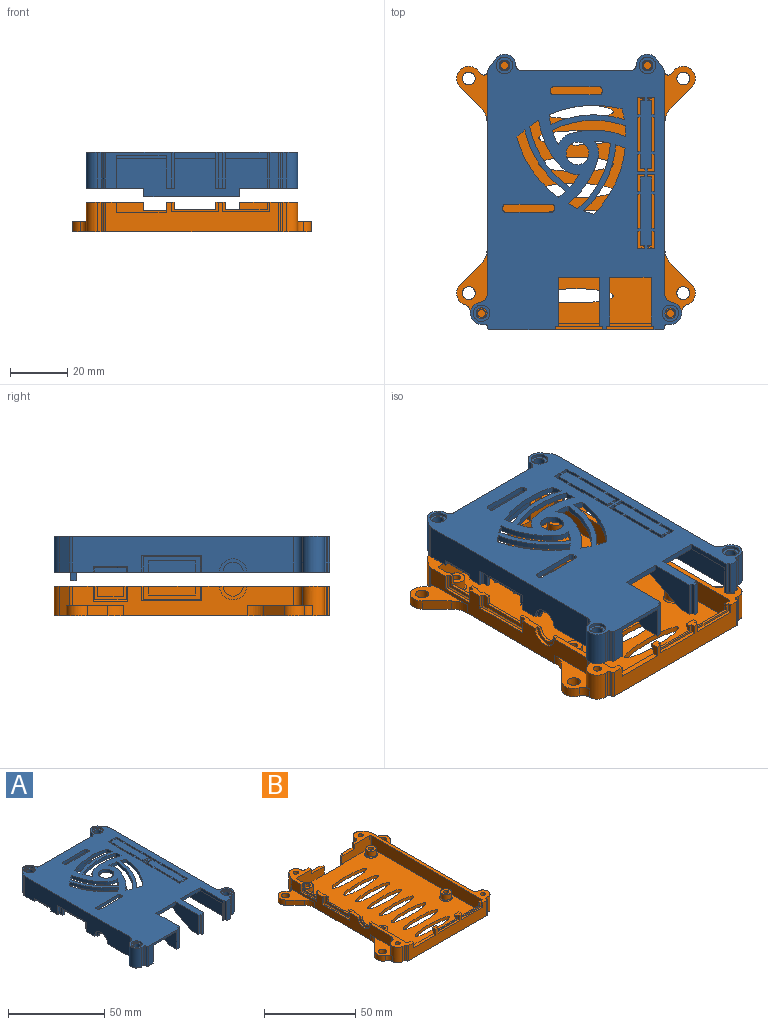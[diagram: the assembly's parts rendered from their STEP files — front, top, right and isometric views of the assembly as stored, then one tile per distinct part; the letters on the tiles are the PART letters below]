
ASSEMBLY  parts=2 mates=1
PART A: 207 faces, bbox 73.8x96.3x15.5 mm
  f0: plane 96.25x73.8mm, normal (0,0,1), area 4343.7mm2, adj f1,f2,f3,f4,f5,f6,f8,f9
  f1: cylinder r=38.11mm len=2.81mm, axis (0,0,1), area 7.6mm2, adj f0,f3,f6,f7
  f2: cylinder r=38.11mm len=3.17mm, axis (0,0,1), area 7.6mm2, adj f0,f7,f27,f28
  f3: cylinder r=34.77mm len=21.39mm, axis (0,0,-1), area 52.8mm2, adj f0,f1,f4,f7
  f4: cylinder r=25.5mm len=2.73mm, axis (0,0,1), area 7mm2, adj f0,f3,f6,f7
  f5: cylinder r=25.5mm len=4.42mm, axis (0,0,1), area 11.1mm2, adj f0,f7,f27,f29
  f6: cylinder r=38.11mm len=21mm, axis (0,0,1), area 52mm2, adj f0,f1,f4,f7
  f7: plane 86.6x58mm, normal (0,0,-1), area 3024.7mm2, adj f1,f2,f3,f4,f5,f6,f8,f9
  f8: cylinder r=38.11mm len=3.71mm, axis (0,0,1), area 7.6mm2, adj f0,f7,f10,f13
  f9: cylinder r=38.11mm len=3.78mm, axis (0,0,1), area 7.6mm2, adj f0,f7,f14,f16
  f10: cylinder r=34.77mm len=25.71mm, axis (0,0,-1), area 52.8mm2, adj f0,f7,f8,f11
  f11: cylinder r=25.5mm len=3.44mm, axis (0,0,1), area 7mm2, adj f0,f7,f10,f13
  f12: cylinder r=25.5mm len=5.08mm, axis (0,0,1), area 11.1mm2, adj f0,f7,f14,f15
  f13: cylinder r=38.11mm len=25.42mm, axis (0,0,1), area 52mm2, adj f0,f7,f8,f11
  f14: cylinder r=32.83mm len=25.5mm, axis (0,0,-1), area 52.5mm2, adj f0,f7,f9,f12
  f15: cylinder r=7.38mm len=4.78mm, axis (0,0,1), area 12.9mm2, adj f0,f7,f12,f16
  f16: cylinder r=29.38mm len=18.77mm, axis (0,0,1), area 38.3mm2, adj f0,f7,f9,f15
  f17: cylinder r=38.11mm len=3.62mm, axis (0,0,1), area 7.6mm2, adj f0,f7,f19,f22
  f18: cylinder r=38.11mm len=3.38mm, axis (0,0,1), area 7.6mm2, adj f0,f7,f23,f25
  f19: cylinder r=34.77mm len=23.14mm, axis (0,0,-1), area 52.8mm2, adj f0,f7,f17,f20
  f20: cylinder r=25.5mm len=3.24mm, axis (0,0,1), area 7mm2, adj f0,f7,f19,f22
  f21: cylinder r=25.5mm len=5.48mm, axis (0,0,1), area 11.1mm2, adj f0,f7,f23,f24
  f22: cylinder r=38.11mm len=23.03mm, axis (0,0,1), area 52mm2, adj f0,f7,f17,f20
  f23: cylinder r=32.83mm len=22.84mm, axis (0,0,-1), area 52.5mm2, adj f0,f7,f18,f21
  f24: cylinder r=7.38mm len=6.15mm, axis (0,0,1), area 12.9mm2, adj f0,f7,f21,f25
  f25: cylinder r=29.38mm len=15.65mm, axis (0,0,1), area 38.3mm2, adj f0,f7,f18,f24
  f26: cylinder r=4mm len=8mm, axis (0,0,1), area 50.3mm2, adj f0,f7
  f27: cylinder r=32.83mm len=21.32mm, axis (0,0,-1), area 52.5mm2, adj f0,f2,f5,f7
  f28: cylinder r=29.38mm len=16.85mm, axis (0,0,1), area 38.3mm2, adj f0,f2,f7,f29
  f29: cylinder r=7.38mm len=5.88mm, axis (0,0,1), area 12.9mm2, adj f0,f5,f7,f28
  f30: plane 16x2mm, normal (0,-1,0), area 32mm2, adj f0,f7,f31,f37
  f31: cylinder r=1mm len=2mm, axis (0,0,-1), area 3.1mm2, adj f0,f7,f30,f32
  f32: plane 2x0.8mm, normal (-1,0,0), area 1.6mm2, adj f0,f7,f31,f33
  f33: cylinder r=1mm len=2mm, axis (0,0,-1), area 3.1mm2, adj f0,f7,f32,f34
  f34: plane 16x2mm, normal (0,1,0), area 32mm2, adj f0,f7,f33,f35
  f35: cylinder r=1mm len=2mm, axis (0,0,-1), area 3.1mm2, adj f0,f7,f34,f36
  f36: plane 2x0.8mm, normal (1,0,0), area 1.6mm2, adj f0,f7,f35,f37
  f37: cylinder r=1mm len=2mm, axis (0,0,-1), area 3.1mm2, adj f0,f7,f30,f36
  f38: plane 2x0.8mm, normal (-1,0,0), area 1.6mm2, adj f0,f7,f39,f45
  f39: cylinder r=1mm len=2mm, axis (0,0,-1), area 3.1mm2, adj f0,f7,f38,f40
  f40: plane 16x2mm, normal (0,1,0), area 32mm2, adj f0,f7,f39,f41
  f41: cylinder r=1mm len=2mm, axis (0,0,-1), area 3.1mm2, adj f0,f7,f40,f42
  f42: plane 2x0.8mm, normal (1,0,0), area 1.6mm2, adj f0,f7,f41,f43
  f43: cylinder r=1mm len=2mm, axis (0,0,-1), area 3.1mm2, adj f0,f7,f42,f44
  f44: plane 16x2mm, normal (0,-1,0), area 32mm2, adj f0,f7,f43,f45
  f45: cylinder r=1mm len=2mm, axis (0,0,-1), area 3.1mm2, adj f0,f7,f38,f44
  f46: cylinder r=1mm len=10.5mm, axis (0,0,-1), area 16.5mm2, adj f7,f47,f50,f55
  f47: plane 10.5x1.55mm, normal (0,1,0), area 16.3mm2, adj f7,f46,f50,f90
  f48: plane 10.5x1.75mm, normal (0,1,0), area 18.4mm2, adj f7,f51,f60,f100
  f49: plane 9.75x2.5mm, normal (0,0,-1), area 16.8mm2, adj f55,f104,f110,f111,f112,f113,f114,f115
  f50: plane 30.25x10.45mm, normal (0,0,-1), area 94.5mm2, adj f46,f47,f55,f82,f90,f103,f104,f105
  f51: plane 96.25x20.3mm, normal (0,0,-1), area 270.9mm2, adj f48,f57,f58,f59,f60,f61,f62,f69
  f52: plane 32.75x14.2mm, normal (0,0,-1), area 96.1mm2, adj f55,f56,f57,f62,f68,f104,f115,f116
  f53: plane 6x3.5mm, normal (0,0,-1), area 18.6mm2, adj f80,f83,f85,f93,f94,f95,f96,f98
  f54: plane 6x2.8mm, normal (0,0,-1), area 15.6mm2, adj f82,f84,f86,f87,f88,f102
  f55: plane 84.6x10.5mm, normal (1,0,0), area 682.2mm2, adj f7,f46,f49,f50,f52,f56,f112,f122
  f56: cylinder r=1mm len=10.5mm, axis (0,0,1), area 16.5mm2, adj f7,f52,f55,f57
  f57: plane 56x13.5mm, normal (0,-1,0), area 688.2mm2, adj f7,f51,f52,f56,f58,f61,f64,f68
  f58: cylinder r=1mm len=10.5mm, axis (0,0,1), area 16.5mm2, adj f7,f51,f57,f59
  f59: plane 84.6x10.5mm, normal (-1,0,0), area 888.3mm2, adj f7,f51,f58,f60
  f60: cylinder r=1mm len=10.5mm, axis (0,0,1), area 16.5mm2, adj f7,f48,f51,f59
  f61: plane 3x2mm, normal (1,0,0), area 6mm2, adj f51,f57,f62,f64
  f62: plane 38.21x15.5mm, normal (0,1,0), area 553.1mm2, adj f0,f51,f52,f61,f63,f64,f66,f67
  f63: plane 1.5x1mm, normal (1,0,0), area 1.5mm2, adj f62,f64,f65,f67
  f64: plane 33.4x2mm, normal (0,0,-1), area 50.3mm2, adj f57,f61,f62,f63,f65,f66,f68
  f65: plane 16.5x1.5mm, normal (0,1,0), area 24.7mm2, adj f63,f64,f66,f67
  f66: plane 1.5x1mm, normal (-1,0,0), area 1.5mm2, adj f62,f64,f65,f67
  f67: plane 16.5x1mm, normal (0,0,-1), area 16.5mm2, adj f62,f63,f65,f66
  f68: plane 3x2mm, normal (-1,0,0), area 6mm2, adj f52,f57,f62,f64
  f69: cylinder r=2mm len=12.5mm, axis (0,0,1), area 38.2mm2, adj f0,f51,f62,f70
  f70: cylinder r=3.9mm len=12.5mm, axis (0,0,1), area 121.2mm2, adj f0,f51,f69,f71
  f71: plane 12.5x3.48mm, normal (0.82,0.58,0), area 53.1mm2, adj f0,f51,f70,f72
  f72: cylinder r=2mm len=12.5mm, axis (0,0,1), area 15.3mm2, adj f0,f51,f71,f73
  f73: plane 77.46x12.5mm, normal (1,0,0), area 968.2mm2, adj f0,f51,f72,f75
  f74: plane 12.5x0.18mm, normal (1,0,0), area 2.3mm2, adj f0,f51,f78,f79
  f75: cylinder r=3mm len=12.5mm, axis (0,0,1), area 53.5mm2, adj f0,f51,f73,f76
  f76: cylinder r=3.9mm len=12.5mm, axis (0,0,1), area 146.1mm2, adj f0,f51,f75,f77
  f77: plane 12.5x1.2mm, normal (0,-1,0), area 15mm2, adj f0,f51,f76,f78
  f78: cylinder r=0.8mm len=12.5mm, axis (0,0,-1), area 15.7mm2, adj f0,f51,f74,f77
  f79: cylinder r=0.8mm len=12.5mm, axis (0,0,-1), area 15.7mm2, adj f0,f51,f74,f81
  f80: plane 12.5x1.5mm, normal (0,-1,0), area 18.8mm2, adj f0,f53,f83,f98
  f81: plane 12.5x2.95mm, normal (0,-1,0), area 36.9mm2, adj f0,f51,f79,f99
  f82: plane 22.95x12.5mm, normal (0,-1,0), area 90.3mm2, adj f0,f50,f54,f88,f90,f91,f102,f103
  f83: plane 12.5x1.2mm, normal (-1,0,0), area 15mm2, adj f0,f53,f80,f85
  f84: plane 12.5x1mm, normal (0,-1,0), area 12.5mm2, adj f0,f54,f86,f102
  f85: plane 12.5x1mm, normal (0,-1,0), area 12.5mm2, adj f0,f53,f83,f93
  f86: plane 25.8x12.5mm, normal (1,0,0), area 194.7mm2, adj f0,f7,f54,f84,f87,f92
  f87: plane 21x10.5mm, normal (0,0.45,-0.89), area 65.7mm2, adj f7,f54,f86,f88
  f88: plane 27x11.3mm, normal (-1,0,0), area 191.4mm2, adj f7,f54,f82,f87,f89,f91
  f89: plane 17.4x0.8mm, normal (0,-1,0), area 13.9mm2, adj f7,f88,f90,f91
  f90: plane 22.7x11.3mm, normal (1,0,0), area 39.2mm2, adj f7,f47,f50,f82,f89,f91
  f91: plane 22.7x17.4mm, normal (0,0,-1), area 395mm2, adj f82,f88,f89,f90
  f92: plane 14.5x2mm, normal (0,-1,0), area 29mm2, adj f0,f7,f86,f93
  f93: plane 25.8x12.5mm, normal (-1,0,0), area 194.7mm2, adj f0,f7,f53,f85,f92,f94
  f94: plane 21x10.5mm, normal (0,0.45,-0.89), area 82.2mm2, adj f7,f53,f93,f95
  f95: plane 25.8x12.5mm, normal (1,0,0), area 194.7mm2, adj f0,f7,f53,f94,f96,f101
  f96: plane 12.5x1mm, normal (0,-1,0), area 12.5mm2, adj f0,f53,f95,f98
  f97: plane 12.5x1mm, normal (0,-1,0), area 12.5mm2, adj f0,f51,f99,f100
  f98: plane 12.5x1.2mm, normal (1,0,0), area 15mm2, adj f0,f53,f80,f96
  f99: plane 12.5x1.2mm, normal (-1,0,0), area 15mm2, adj f0,f51,f81,f97
  f100: plane 17.05x12.5mm, normal (-1,0,0), area 42.5mm2, adj f0,f7,f48,f51,f97,f101
  f101: plane 14.5x2mm, normal (0,-1,0), area 29mm2, adj f0,f7,f95,f100
  f102: plane 12.5x1.2mm, normal (1,0,0), area 15mm2, adj f0,f54,f82,f84
  f103: cylinder r=0.8mm len=12.5mm, axis (0,0,1), area 15.7mm2, adj f0,f50,f82,f105
  f104: plane 77.46x12.5mm, normal (-1,0,0), area 784.3mm2, adj f0,f49,f50,f52,f106,f110,f113,f117
  f105: plane 12.5x0.18mm, normal (-1,0,0), area 2.2mm2, adj f0,f50,f103,f109
  f106: cylinder r=3mm len=12.5mm, axis (0,0,-1), area 53.5mm2, adj f0,f50,f104,f107
  f107: cylinder r=3.9mm len=12.5mm, axis (0,0,1), area 146.1mm2, adj f0,f50,f106,f108
  f108: plane 12.5x1.2mm, normal (0,-1,0), area 15mm2, adj f0,f50,f107,f109
  f109: cylinder r=0.8mm len=12.5mm, axis (0,0,1), area 15.7mm2, adj f0,f50,f105,f108
  f110: cylinder r=4.75mm len=9.5mm, axis (-1,0,0), area 14.9mm2, adj f49,f50,f104,f111
  f111: plane 9.5x4.75mm, normal (-1,0,0), area 16.2mm2, adj f49,f50,f110,f112
  f112: cylinder r=3.5mm len=7mm, axis (-1,0,0), area 11mm2, adj f49,f50,f55,f111
  f113: plane 5.93x1mm, normal (0,1,0), area 5.9mm2, adj f49,f104,f114,f118
  f114: plane 5.93x0.5mm, normal (-0.71,0.71,0), area 4mm2, adj f49,f113,f115,f119
  f115: plane 20x5.43mm, normal (-1,0,0), area 43.8mm2, adj f49,f52,f114,f116,f119,f120,f125,f126
  f116: plane 5.93x0.5mm, normal (-0.71,-0.71,0), area 4mm2, adj f52,f115,f117,f119
  f117: plane 5.93x1mm, normal (0,-1,0), area 5.9mm2, adj f52,f104,f116,f118
  f118: plane 21x1mm, normal (0,0,-1), area 21mm2, adj f104,f113,f117,f119
  f119: plane 21x0.5mm, normal (-0.71,0,-0.71), area 14.5mm2, adj f114,f115,f116,f118
  f120: plane 3.93x1mm, normal (0,1,0), area 3.9mm2, adj f49,f115,f121,f126
  f121: plane 23x5.93mm, normal (1,0,0), area 71.5mm2, adj f49,f52,f120,f122,f123,f124,f125,f126
  f122: plane 6.43x0.5mm, normal (0.71,-0.71,0), area 4.4mm2, adj f49,f55,f121,f123
  f123: plane 24x0.5mm, normal (0.71,0,0.71), area 16.6mm2, adj f55,f121,f122,f124
  f124: plane 6.43x0.5mm, normal (0.71,0.71,0), area 4.4mm2, adj f52,f55,f121,f123
  f125: plane 3.93x1mm, normal (0,-1,0), area 3.9mm2, adj f52,f115,f121,f126
  f126: plane 16.5x1mm, normal (0,0,-1), area 16.5mm2, adj f115,f120,f121,f125
  f127: plane 2x1mm, normal (0,1,0), area 2mm2, adj f52,f104,f128,f132
  f128: plane 2x0.5mm, normal (-0.71,0.71,0), area 1.2mm2, adj f52,f127,f129,f133
  f129: plane 11x1.5mm, normal (-1,0,0), area 16.5mm2, adj f52,f128,f130,f133
  f130: plane 2x0.5mm, normal (-0.71,-0.71,0), area 1.2mm2, adj f52,f129,f131,f133
  f131: plane 2x1mm, normal (0,-1,0), area 2mm2, adj f52,f104,f130,f132
  f132: plane 12x1mm, normal (0,0,-1), area 12mm2, adj f104,f127,f131,f133
  f133: plane 12x0.5mm, normal (-0.71,0,-0.71), area 8.1mm2, adj f128,f129,f130,f132
  f134: cylinder r=2mm len=12.5mm, axis (0,0,-1), area 15.3mm2, adj f0,f52,f104,f135
  f135: plane 12.5x3.48mm, normal (-0.82,0.58,0), area 53.1mm2, adj f0,f52,f134,f136
  f136: cylinder r=3.9mm len=12.5mm, axis (0,0,1), area 121.2mm2, adj f0,f52,f135,f137
  f137: cylinder r=2mm len=12.5mm, axis (0,0,-1), area 38.2mm2, adj f0,f52,f62,f136
  f138: plane 2.5x0.5mm, normal (0.71,0.71,0), area 1.6mm2, adj f52,f55,f139,f141
  f139: plane 12x2mm, normal (1,0,0), area 24mm2, adj f52,f138,f140,f141
  f140: plane 2.5x0.5mm, normal (0.71,-0.71,0), area 1.6mm2, adj f52,f55,f139,f141
  f141: plane 13x0.5mm, normal (0.71,0,0.71), area 8.8mm2, adj f55,f138,f139,f140
  f142: cylinder r=1.9mm len=11.5mm, axis (0,0,1), area 137.3mm2, adj f51,f145
  f143: plane 5.8x5.8mm, normal (0,0,1), area 15.1mm2, adj f147,f153
  f144: plane 5.8x5.8mm, normal (0,0,1), area 15.1mm2, adj f148,f152
  f145: plane 5.8x5.8mm, normal (0,0,1), area 15.1mm2, adj f142,f149
  f146: plane 5.8x5.8mm, normal (0,0,1), area 15.1mm2, adj f150,f151
  f147: cylinder r=2.9mm len=5.8mm, axis (0,0,1), area 18.2mm2, adj f0,f143
  f148: cylinder r=2.9mm len=5.8mm, axis (0,0,1), area 18.2mm2, adj f0,f144
  f149: cylinder r=2.9mm len=5.8mm, axis (0,0,1), area 18.2mm2, adj f0,f145
  f150: cylinder r=2.9mm len=5.8mm, axis (0,0,1), area 18.2mm2, adj f0,f146
  f151: cylinder r=1.9mm len=11.5mm, axis (0,0,1), area 137.3mm2, adj f50,f146
  f152: cylinder r=1.9mm len=11.5mm, axis (0,0,-1), area 137.3mm2, adj f51,f144
  f153: cylinder r=1.9mm len=11.5mm, axis (0,0,-1), area 137.3mm2, adj f52,f143
  f154: plane 6x2mm, normal (0,1,0), area 11mm2, adj f0,f7,f155,f161,f174,f186,f198
  f155: plane 52.7x6mm, normal (0,0,-1), area 208.8mm2, adj f154,f156,f157,f158,f159,f160,f161,f162
  f156: plane 2.5x1mm, normal (0,1,0), area 2.5mm2, adj f0,f155,f157,f161
  f157: plane 1x1mm, normal (-1,0,0), area 1mm2, adj f0,f155,f156,f158
  f158: plane 1.5x1mm, normal (0,-1,0), area 1.5mm2, adj f0,f155,f157,f159
  f159: plane 4.96x1mm, normal (-1,0,0), area 5mm2, adj f0,f155,f158,f160
  f160: plane 1x1mm, normal (0,-1,0), area 1mm2, adj f0,f155,f159,f161
  f161: plane 52.7x2mm, normal (1,0,0), area 100.4mm2, adj f0,f7,f154,f155,f156,f160,f162,f164
  f162: plane 1x1mm, normal (0,1,0), area 1mm2, adj f0,f155,f161,f163
  f163: plane 11.93x1mm, normal (-1,0,0), area 11.9mm2, adj f0,f155,f162,f164
  f164: plane 1x1mm, normal (0,-1,0), area 1mm2, adj f0,f155,f161,f163
  f165: plane 1x1mm, normal (0,1,0), area 1mm2, adj f0,f155,f161,f166
  f166: plane 4.96x1mm, normal (-1,0,0), area 5mm2, adj f0,f155,f165,f167
  f167: plane 1.5x1mm, normal (0,1,0), area 1.5mm2, adj f0,f155,f166,f168
  f168: plane 1x1mm, normal (-1,0,0), area 1mm2, adj f0,f155,f167,f169
  f169: plane 6x2mm, normal (0,-1,0), area 11mm2, adj f0,f7,f155,f161,f168,f170,f174
  f170: plane 1x1mm, normal (1,0,0), area 1mm2, adj f0,f155,f169,f171
  f171: plane 1.5x1mm, normal (0,1,0), area 1.5mm2, adj f0,f155,f170,f172
  f172: plane 4.96x1mm, normal (1,0,0), area 5mm2, adj f0,f155,f171,f173
  f173: plane 1x1mm, normal (0,1,0), area 1mm2, adj f0,f155,f172,f174
  f174: plane 52.7x2mm, normal (-1,0,0), area 100.4mm2, adj f0,f7,f154,f155,f169,f173,f175,f179
  f175: plane 2.5x1mm, normal (0,-1,0), area 2.5mm2, adj f0,f155,f174,f176
  f176: plane 1x1mm, normal (1,0,0), area 1mm2, adj f0,f155,f175,f177
  f177: plane 1.5x1mm, normal (0,1,0), area 1.5mm2, adj f0,f155,f176,f178
  f178: plane 4.96x1mm, normal (1,0,0), area 5mm2, adj f0,f155,f177,f179
  f179: plane 1x1mm, normal (0,1,0), area 1mm2, adj f0,f155,f174,f178
  f180: plane 1x1mm, normal (0,-1,0), area 1mm2, adj f0,f155,f174,f181
  f181: plane 11.93x1mm, normal (1,0,0), area 11.9mm2, adj f0,f155,f180,f182
  f182: plane 1x1mm, normal (0,1,0), area 1mm2, adj f0,f155,f174,f181
  f183: plane 1x1mm, normal (0,-1,0), area 1mm2, adj f0,f155,f174,f184
  f184: plane 4.96x1mm, normal (1,0,0), area 5mm2, adj f0,f155,f183,f185
  f185: plane 1.5x1mm, normal (0,-1,0), area 1.5mm2, adj f0,f155,f184,f186
  f186: plane 1x1mm, normal (1,0,0), area 1mm2, adj f0,f154,f155,f185
  f187: plane 1x1mm, normal (0,-1,0), area 1mm2, adj f0,f155,f174,f188
  f188: plane 11.93x1mm, normal (1,0,0), area 11.9mm2, adj f0,f155,f187,f189
  f189: plane 1x1mm, normal (0,1,0), area 1mm2, adj f0,f155,f174,f188
  f190: plane 1x1mm, normal (0,-1,0), area 1mm2, adj f0,f155,f174,f191
  f191: plane 4.96x1mm, normal (1,0,0), area 5mm2, adj f0,f155,f190,f192
  f192: plane 1.5x1mm, normal (0,-1,0), area 1.5mm2, adj f0,f155,f191,f193
  f193: plane 1x1mm, normal (1,0,0), area 1mm2, adj f0,f155,f192,f194
  f194: plane 2.5x1mm, normal (0,1,0), area 2.5mm2, adj f0,f155,f174,f193
  f195: plane 1x1mm, normal (0,-1,0), area 1mm2, adj f0,f155,f161,f196
  f196: plane 4.96x1mm, normal (-1,0,0), area 5mm2, adj f0,f155,f195,f197
  f197: plane 1.5x1mm, normal (0,-1,0), area 1.5mm2, adj f0,f155,f196,f198
  f198: plane 1x1mm, normal (-1,0,0), area 1mm2, adj f0,f154,f155,f197
  f199: plane 1x1mm, normal (0,1,0), area 1mm2, adj f0,f155,f161,f200
  f200: plane 11.93x1mm, normal (-1,0,0), area 11.9mm2, adj f0,f155,f199,f201
  f201: plane 1x1mm, normal (0,-1,0), area 1mm2, adj f0,f155,f161,f200
  f202: plane 1x1mm, normal (0,1,0), area 1mm2, adj f0,f155,f161,f203
  f203: plane 4.96x1mm, normal (-1,0,0), area 5mm2, adj f0,f155,f202,f204
  f204: plane 1.5x1mm, normal (0,1,0), area 1.5mm2, adj f0,f155,f203,f205
  f205: plane 1x1mm, normal (-1,0,0), area 1mm2, adj f0,f155,f204,f206
  f206: plane 2.5x1mm, normal (0,-1,0), area 2.5mm2, adj f0,f155,f161,f205
PART B: 170 faces, bbox 83.8x96.6x10.6 mm
  f0: plane 96.58x83.83mm, normal (0,0,-1), area 5317.9mm2, adj f1,f6,f7,f8,f9,f37,f38,f39
  f1: cylinder r=2.25mm len=4.5mm, axis (0,0,-1), area 49.5mm2, adj f0,f3
  f2: plane 22.79x10.75mm, normal (0,0,1), area 100.2mm2, adj f8,f9,f93,f123,f124,f125,f126,f127
  f3: plane 22.79x10.75mm, normal (0,0,1), area 100.2mm2, adj f1,f39,f152,f153,f154,f155,f156,f157
  f4: plane 20.07x10.76mm, normal (0,0,1), area 93.7mm2, adj f6,f39,f41,f147,f148,f149,f150,f151
  f5: plane 20.07x10.76mm, normal (0,0,1), area 93.7mm2, adj f7,f93,f128,f129,f130,f131,f132,f133
  f6: cylinder r=2.25mm len=4.5mm, axis (0,0,-1), area 49.5mm2, adj f0,f4
  f7: cylinder r=2.25mm len=4.5mm, axis (0,0,-1), area 49.5mm2, adj f0,f5
  f8: cylinder r=2.25mm len=4.5mm, axis (0,0,-1), area 49.5mm2, adj f0,f2
  f9: cylinder r=3.9mm len=10.3mm, axis (0,0,-1), area 101.4mm2, adj f0,f2,f12,f123,f127,f139
  f10: plane 3x2.8mm, normal (0,0,1), area 7.2mm2, adj f25,f28,f30,f37,f162,f163
  f11: plane 3.5x3mm, normal (0,0,1), area 8.1mm2, adj f29,f32,f35,f37,f163,f164,f167,f169
  f12: plane 30.25x10.45mm, normal (0,0,1), area 99.5mm2, adj f9,f22,f26,f37,f89,f90,f91,f92
  f13: plane 8.65x2.5mm, normal (0,0,1), area 15.1mm2, adj f89,f93,f95,f96,f97,f98,f100,f101
  f14: plane 9.75x2.5mm, normal (0,0,1), area 16.8mm2, adj f89,f90,f91,f92,f93,f98,f101,f107
  f15: plane 15.1x14.15mm, normal (0,0,1), area 78mm2, adj f17,f46,f82,f88,f89,f93,f97,f99
  f16: plane 96.25x20.25mm, normal (0,0,1), area 280.9mm2, adj f23,f24,f26,f34,f35,f36,f37,f38
  f17: cylinder r=1.4mm len=8.3mm, axis (0,0,-1), area 73mm2, adj f15,f20
  f18: plane 2.8x2.8mm, normal (0,0,1), area 6.2mm2, adj f22
  f19: plane 2.8x2.8mm, normal (0,0,1), area 6.2mm2, adj f23
  f20: plane 2.8x2.8mm, normal (0,0,1), area 6.2mm2, adj f17
  f21: plane 2.8x2.8mm, normal (0,0,1), area 6.2mm2, adj f24
  f22: cylinder r=1.4mm len=8.3mm, axis (0,0,-1), area 73mm2, adj f12,f18
  f23: cylinder r=1.4mm len=8.3mm, axis (0,0,1), area 73mm2, adj f16,f19
  f24: cylinder r=1.4mm len=8.3mm, axis (0,0,-1), area 73mm2, adj f16,f21
  f25: plane 3.6x3mm, normal (-1,0,0), area 8.7mm2, adj f10,f26,f27,f30,f37,f161
  f26: plane 57x8.3mm, normal (0,1,0), area 322.8mm2, adj f12,f16,f25,f27,f28,f31,f32,f33
  f27: plane 2.8x2mm, normal (0,0.89,-0.45), area 6.3mm2, adj f25,f26,f28,f30
  f28: plane 2.55x1.8mm, normal (1,0,0), area 3.5mm2, adj f10,f26,f27,f30,f163,f168
  f29: plane 3.5x0.55mm, normal (0,1,0), area 1.9mm2, adj f11,f31,f32,f169
  f30: plane 2.8x0.55mm, normal (0,1,0), area 1.5mm2, adj f10,f25,f27,f28
  f31: plane 3.5x2mm, normal (0,0.89,-0.45), area 7.8mm2, adj f26,f29,f32,f169
  f32: plane 2.55x1.8mm, normal (1,0,0), area 3.5mm2, adj f11,f26,f29,f31,f33,f35
  f33: plane 14.5x0.8mm, normal (0,0,1), area 11.6mm2, adj f26,f32,f34,f35
  f34: plane 2.47x0.8mm, normal (-1,0,0), area 2mm2, adj f16,f26,f33,f35
  f35: plane 16.5x3.17mm, normal (0,-1,0), area 16.5mm2, adj f11,f16,f32,f33,f34,f36,f166,f167
  f36: plane 3.17x1.2mm, normal (-1,0,0), area 3.8mm2, adj f16,f35,f37,f166
  f37: plane 60.4x10.3mm, normal (0,-1,0), area 454.9mm2, adj f0,f10,f11,f12,f16,f25,f36,f38
  f38: cylinder r=0.8mm len=10.3mm, axis (0,0,-1), area 12.9mm2, adj f0,f16,f37,f40
  f39: plane 77.46x10.3mm, normal (1,0,0), area 678.5mm2, adj f0,f3,f4,f16,f41,f151,f152,f157
  f40: plane 10.3x0.18mm, normal (1,0,0), area 1.9mm2, adj f0,f16,f38,f159
  f41: cylinder r=2mm len=10.3mm, axis (0,0,1), area 12.1mm2, adj f0,f4,f16,f39,f42,f147
  f42: plane 10.3x3.48mm, normal (0.82,0.58,0), area 43.8mm2, adj f0,f16,f41,f43
  f43: cylinder r=3.9mm len=10.3mm, axis (0,0,-1), area 99.9mm2, adj f0,f16,f42,f44
  f44: cylinder r=2mm len=10.3mm, axis (0,0,1), area 31.5mm2, adj f0,f16,f43,f45
  f45: plane 10.96x10.3mm, normal (0,1,0), area 87.3mm2, adj f0,f16,f44,f47,f83,f84
  f46: plane 10.76x10.3mm, normal (0,1,0), area 85.3mm2, adj f0,f15,f136,f141,f142,f146
  f47: plane 7.3x1mm, normal (-1,0,0), area 7.3mm2, adj f0,f45,f48,f83
  f48: plane 7.3x1.5mm, normal (0,1,0), area 10.9mm2, adj f0,f47,f50,f83
  f49: plane 7.3x1.5mm, normal (0,1,0), area 11mm2, adj f0,f142,f143,f146
  f50: plane 7.3x1mm, normal (-1,0,0), area 7.3mm2, adj f0,f48,f51,f81,f83
  f51: cylinder r=0.5mm len=2mm, axis (0,0,-1), area 1.6mm2, adj f0,f50,f52,f145
  f52: plane 86.93x58.33mm, normal (0,0,1), area 4054.4mm2, adj f26,f51,f53,f54,f55,f56,f57,f58
  f53: extruded ~26x5mm, area 109.1mm2, adj f0,f52
  f54: extruded ~26x5mm, area 109.1mm2, adj f0,f52
  f55: extruded ~26x5mm, area 109.1mm2, adj f0,f52
  f56: extruded ~26x5mm, area 109.1mm2, adj f0,f52
  f57: extruded ~26x5mm, area 109.1mm2, adj f0,f52
  f58: extruded ~26x5mm, area 109.1mm2, adj f0,f52
  f59: extruded ~26x5mm, area 109.1mm2, adj f0,f52
  f60: extruded ~26x5mm, area 109.1mm2, adj f0,f52
  f61: cone r=3.15mm half-angle=45deg, axis (0,0,-1), area 14mm2, adj f52,f62
  f62: cylinder r=2.9mm len=5.8mm, axis (0,0,1), area 63.8mm2, adj f61,f64
  f63: plane 5.8x5.8mm, normal (0,0,1), area 20.3mm2, adj f67,f69
  f64: plane 5.8x5.8mm, normal (0,0,1), area 20.3mm2, adj f62,f74
  f65: plane 5.8x5.8mm, normal (0,0,1), area 20.3mm2, adj f76,f77
  f66: plane 5.8x5.8mm, normal (0,0,1), area 20.3mm2, adj f75,f79
  f67: cylinder r=2.9mm len=5.8mm, axis (0,0,1), area 63.8mm2, adj f63,f68
  f68: cone r=3.15mm half-angle=45deg, axis (0,0,-1), area 14mm2, adj f52,f67
  f69: cylinder r=1.4mm len=5mm, axis (0,0,1), area 44mm2, adj f63,f72
  f70: plane 2.8x2.8mm, normal (0,0,1), area 6.2mm2, adj f74
  f71: plane 2.8x2.8mm, normal (0,0,1), area 6.2mm2, adj f75
  f72: plane 2.8x2.8mm, normal (0,0,1), area 6.2mm2, adj f69
  f73: plane 2.8x2.8mm, normal (0,0,1), area 6.2mm2, adj f76
  f74: cylinder r=1.4mm len=5mm, axis (0,0,1), area 44mm2, adj f64,f70
  f75: cylinder r=1.4mm len=5mm, axis (0,0,1), area 44mm2, adj f66,f71
  f76: cylinder r=1.4mm len=5mm, axis (0,0,1), area 44mm2, adj f65,f73
  f77: cylinder r=2.9mm len=5.8mm, axis (0,0,1), area 63.8mm2, adj f65,f78
  f78: cone r=3.15mm half-angle=45deg, axis (0,0,-1), area 14mm2, adj f52,f77
  f79: cylinder r=2.9mm len=5.8mm, axis (0,0,1), area 63.8mm2, adj f66,f80
  f80: cone r=3.15mm half-angle=45deg, axis (0,0,-1), area 14mm2, adj f52,f79
  f81: plane 21.85x8.3mm, normal (0,-1,0), area 151.4mm2, adj f16,f50,f52,f83,f84,f85
  f82: plane 21.65x8.3mm, normal (0,-1,0), area 149.7mm2, adj f15,f52,f88,f141,f142,f143
  f83: plane 10x2mm, normal (0,0,1), area 18.5mm2, adj f45,f47,f48,f50,f81,f84
  f84: plane 3x2mm, normal (-1,0,0), area 6mm2, adj f16,f45,f81,f83
  f85: cylinder r=0.5mm len=8.3mm, axis (0,0,1), area 6.5mm2, adj f16,f52,f81,f86
  f86: plane 85.6x8.3mm, normal (-1,0,0), area 710.5mm2, adj f16,f52,f85,f87
  f87: cylinder r=0.5mm len=8.3mm, axis (0,0,1), area 6.5mm2, adj f16,f26,f52,f86
  f88: cylinder r=0.5mm len=8.3mm, axis (0,0,1), area 6.5mm2, adj f15,f52,f82,f89
  f89: plane 85.6x8.3mm, normal (1,0,0), area 494.1mm2, adj f12,f13,f14,f15,f52,f88,f90,f102
  f90: cylinder r=3.5mm len=7mm, axis (-1,0,0), area 11mm2, adj f12,f14,f89,f91
  f91: plane 9.5x4.75mm, normal (-1,0,0), area 16.2mm2, adj f12,f14,f90,f92
  f92: cylinder r=4.75mm len=9.5mm, axis (-1,0,0), area 14.9mm2, adj f12,f14,f91,f93
  f93: plane 77.46x10.3mm, normal (-1,0,0), area 472.5mm2, adj f0,f2,f5,f12,f13,f14,f15,f92
  f94: plane 10.3x0.18mm, normal (-1,0,0), area 1.9mm2, adj f0,f12,f137,f138
  f95: plane 5.12x1mm, normal (0,-1,0), area 5.1mm2, adj f13,f93,f96,f121
  f96: plane 5.12x0.5mm, normal (-0.71,-0.71,0), area 3.4mm2, adj f13,f95,f98,f122
  f97: plane 11x4.75mm, normal (-1,0,0), area 18.5mm2, adj f13,f15,f99,f105,f106,f113,f116,f117
  f98: plane 20x4.62mm, normal (-1,0,0), area 40.9mm2, adj f13,f14,f96,f107,f108,f109,f119,f122
  f99: plane 3.75x1mm, normal (0,-1,0), area 3.8mm2, adj f15,f97,f100,f106
  f100: plane 14x5.25mm, normal (1,0,0), area 39.8mm2, adj f13,f15,f99,f102,f103,f104,f105,f106
  f101: plane 23x3.62mm, normal (1,0,0), area 31.8mm2, adj f13,f14,f107,f108,f109,f110,f111,f112
  f102: plane 5.75x0.5mm, normal (0.71,0.71,0), area 3.9mm2, adj f15,f89,f100,f103
  f103: plane 15x0.5mm, normal (0.71,0,-0.71), area 10.3mm2, adj f89,f100,f102,f104
  f104: plane 5.75x0.5mm, normal (0.71,-0.71,0), area 3.9mm2, adj f13,f89,f100,f103
  f105: plane 3.75x1mm, normal (0,1,0), area 3.8mm2, adj f13,f97,f100,f106
  f106: plane 9x1mm, normal (0,0,1), area 9mm2, adj f97,f99,f100,f105
  f107: plane 3.12x1mm, normal (0,1,0), area 3.1mm2, adj f14,f98,f101,f108
  f108: plane 16.5x1mm, normal (0,0,1), area 16.5mm2, adj f98,f101,f107,f109
  f109: plane 3.12x1mm, normal (0,-1,0), area 3.1mm2, adj f13,f98,f101,f108
  f110: plane 4.62x0.5mm, normal (0.71,0.71,0), area 2.9mm2, adj f13,f89,f101,f111
  f111: plane 24x1mm, normal (0.89,0,-0.45), area 26.3mm2, adj f89,f101,f110,f112
  f112: plane 4.62x0.5mm, normal (0.71,-0.71,0), area 2.9mm2, adj f14,f89,f101,f111
  f113: plane 5.25x0.5mm, normal (-0.71,0.71,0), area 3.5mm2, adj f13,f97,f114,f116
  f114: plane 5.25x1mm, normal (0,1,0), area 5.2mm2, adj f13,f93,f113,f115
  f115: plane 12x1mm, normal (0,0,1), area 12mm2, adj f93,f114,f116,f118
  f116: plane 12x0.5mm, normal (-0.71,0,0.71), area 8.1mm2, adj f97,f113,f115,f117
  f117: plane 5.25x0.5mm, normal (-0.71,-0.71,0), area 3.5mm2, adj f15,f97,f116,f118
  f118: plane 5.25x1mm, normal (0,-1,0), area 5.2mm2, adj f15,f93,f115,f117
  f119: plane 5.12x0.5mm, normal (-0.71,0.71,0), area 3.4mm2, adj f14,f98,f120,f122
  f120: plane 5.12x1mm, normal (0,1,0), area 5.1mm2, adj f14,f93,f119,f121
  f121: plane 21x1mm, normal (0,0,1), area 21mm2, adj f93,f95,f120,f122
  f122: plane 21x0.5mm, normal (-0.71,0,0.71), area 14.5mm2, adj f96,f98,f119,f121
  f123: cylinder r=3mm len=6.8mm, axis (0,0,-1), area 29.1mm2, adj f2,f9,f12,f93
  f124: cylinder r=8mm len=5.66mm, axis (0,0,-1), area 22mm2, adj f0,f2,f93,f125
  f125: plane 7.16x7.16mm, normal (-0.71,0.71,0), area 35.5mm2, adj f0,f2,f124,f126
  f126: cylinder r=4.25mm len=7.02mm, axis (0,0,-1), area 30mm2, adj f0,f2,f125,f127
  f127: cylinder r=3mm len=3.5mm, axis (0,0,-1), area 13.4mm2, adj f0,f2,f9,f126
  f128: cylinder r=8mm len=5.66mm, axis (0,0,1), area 22mm2, adj f0,f5,f93,f129
  f129: plane 7.16x7.16mm, normal (-0.71,-0.71,0), area 35.5mm2, adj f0,f5,f128,f130
  f130: cylinder r=4.25mm len=7.26mm, axis (0,0,-1), area 46.7mm2, adj f0,f5,f129,f131
  f131: plane 3.5x1.45mm, normal (0.71,0.71,0), area 7.2mm2, adj f0,f5,f130,f132
  f132: cylinder r=1.2mm len=3.5mm, axis (0,0,-1), area 9.6mm2, adj f0,f5,f131,f133
  f133: cylinder r=2mm len=10.3mm, axis (0,0,-1), area 12.1mm2, adj f0,f5,f15,f93,f132,f134
  f134: plane 10.3x3.48mm, normal (-0.82,0.58,0), area 43.8mm2, adj f0,f15,f133,f135
  f135: cylinder r=3.9mm len=10.3mm, axis (0,0,-1), area 99.9mm2, adj f0,f15,f134,f136
  f136: cylinder r=2mm len=10.3mm, axis (0,0,-1), area 31.5mm2, adj f0,f15,f46,f135
  f137: cylinder r=0.8mm len=10.3mm, axis (0,0,1), area 12.9mm2, adj f0,f12,f37,f94
  f138: cylinder r=0.8mm len=10.3mm, axis (0,0,1), area 12.9mm2, adj f0,f12,f94,f139
  f139: plane 10.3x1.2mm, normal (0,-1,0), area 12.4mm2, adj f0,f9,f12,f138
  f140: cylinder r=0.5mm len=8.3mm, axis (0,0,-1), area 6.5mm2, adj f12,f26,f52,f89
  f141: plane 3x2mm, normal (1,0,0), area 6mm2, adj f15,f46,f82,f142
  f142: plane 10x2mm, normal (0,0,1), area 18.5mm2, adj f46,f49,f82,f141,f143,f146
  f143: plane 7.3x1mm, normal (1,0,0), area 7.3mm2, adj f0,f49,f82,f142,f144
  f144: cylinder r=0.5mm len=2mm, axis (0,0,-1), area 1.6mm2, adj f0,f52,f143,f145
  f145: plane 12.5x2mm, normal (0,1,0), area 25mm2, adj f0,f51,f52,f144
  f146: plane 7.3x1mm, normal (1,0,0), area 7.3mm2, adj f0,f46,f49,f142
  f147: cylinder r=1.2mm len=3.5mm, axis (0,0,1), area 9.6mm2, adj f0,f4,f41,f148
  f148: plane 3.5x1.45mm, normal (-0.71,0.71,0), area 7.2mm2, adj f0,f4,f147,f149
  f149: cylinder r=4.25mm len=7.26mm, axis (0,0,-1), area 46.7mm2, adj f0,f4,f148,f150
  f150: plane 7.16x7.16mm, normal (0.71,-0.71,0), area 35.5mm2, adj f0,f4,f149,f151
  f151: cylinder r=8mm len=5.66mm, axis (0,0,-1), area 22mm2, adj f0,f4,f39,f150
  f152: cylinder r=8mm len=5.66mm, axis (0,0,1), area 22mm2, adj f0,f3,f39,f153
  f153: plane 7.16x7.16mm, normal (0.71,0.71,0), area 35.5mm2, adj f0,f3,f152,f154
  f154: cylinder r=4.25mm len=7.02mm, axis (0,0,-1), area 30mm2, adj f0,f3,f153,f155
  f155: cylinder r=3mm len=3.5mm, axis (0,0,1), area 13.4mm2, adj f0,f3,f154,f156
  f156: cylinder r=3.9mm len=10.3mm, axis (0,0,1), area 101.4mm2, adj f0,f3,f16,f155,f157,f158
  f157: cylinder r=3mm len=6.8mm, axis (0,0,1), area 29.1mm2, adj f3,f16,f39,f156
  f158: plane 10.3x1.2mm, normal (0,-1,0), area 12.4mm2, adj f0,f16,f156,f159
  f159: cylinder r=0.8mm len=10.3mm, axis (0,0,-1), area 12.9mm2, adj f0,f16,f40,f158
  f160: plane 3.6x2mm, normal (1,0,0), area 7.2mm2, adj f12,f26,f37,f161
  f161: plane 17.4x2mm, normal (0,0,1), area 34.8mm2, adj f25,f26,f37,f160
  f162: plane 3.17x1.2mm, normal (1,0,0), area 3.8mm2, adj f10,f37,f163,f165
  f163: plane 16.5x3.17mm, normal (0,-1,0), area 16.5mm2, adj f10,f11,f28,f162,f164,f165,f168,f169
  f164: plane 3.17x1.2mm, normal (-1,0,0), area 3.8mm2, adj f11,f37,f163,f165
  f165: plane 16.5x1.2mm, normal (0,0,1), area 19.8mm2, adj f37,f162,f163,f164
  f166: plane 16.5x1.2mm, normal (0,0,1), area 19.8mm2, adj f35,f36,f37,f167
  f167: plane 3.17x1.2mm, normal (1,0,0), area 3.8mm2, adj f11,f35,f37,f166
  f168: plane 14.5x0.8mm, normal (0,0,1), area 11.6mm2, adj f26,f28,f163,f169
  f169: plane 2.55x1.8mm, normal (-1,0,0), area 3.5mm2, adj f11,f26,f29,f31,f163,f168
PLACE A t=(-12.26,30.33,56.11)mm
PLACE B t=(-12.26,30.33,30.45)mm
MATE slider B.f9 <-> A.f107  axis (0,0,1) through (-14.26,40.41,40.75)mm
